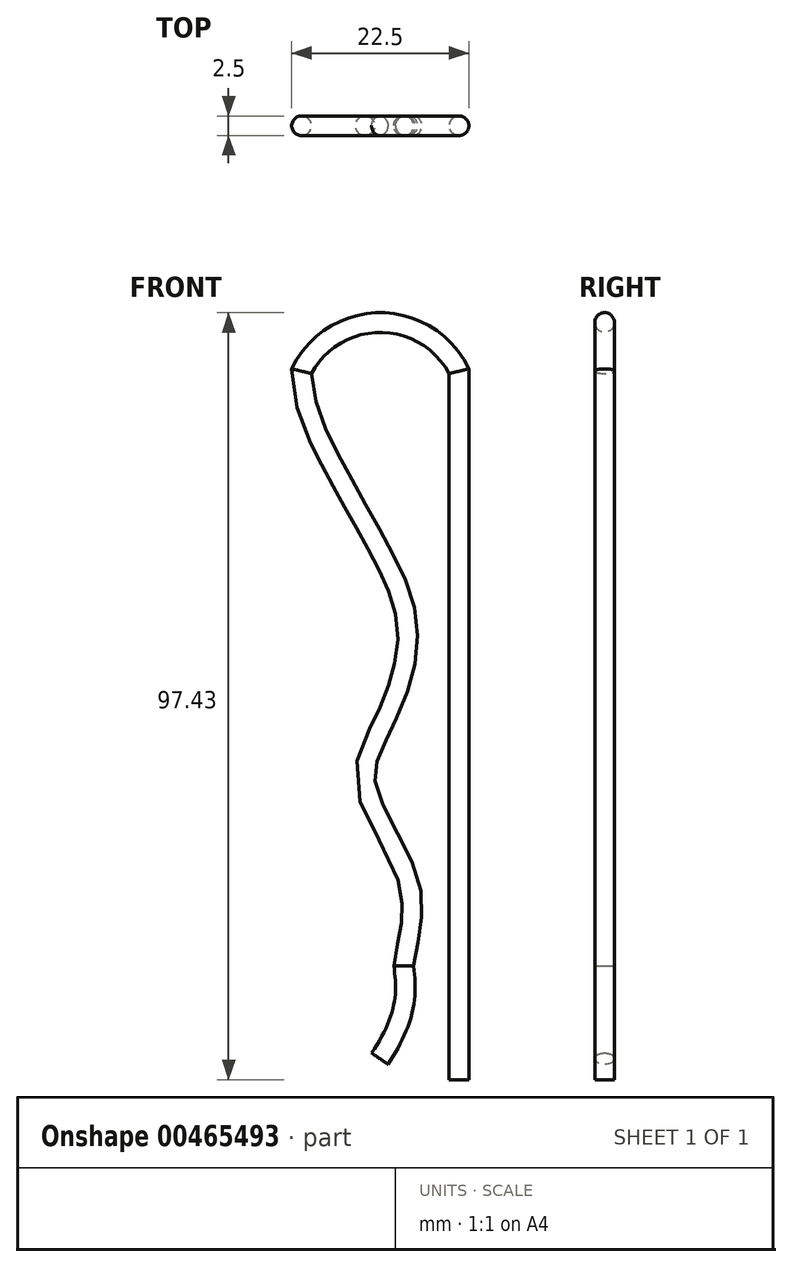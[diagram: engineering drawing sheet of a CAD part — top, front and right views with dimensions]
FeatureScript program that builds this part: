
annotation { "Feature Type Name" : "Feature", "Feature Type Description" : "" }
export const myFeature = defineFeature(function(context is Context, id is Id, definition is map)
    precondition{}
    {
        {
            var Q0;
            Q0=qCreatedBy(makeId("Front.planeOp"),FACE);
            var sketch = newSketch(context, id + "F0", { "sketchPlane" : qUnion([Q0])});
            skLineSegment(sketch, "E0", {"start": v(0, 0) * mm, "end": v(0, 90) * mm});
            skArc(sketch, "E1", {"start": v(0, 90) * mm, "mid": v(-10, 96.18) * mm, "end": v(-20, 90) * mm});
            skFitSpline(sketch, "E2", {"points": [v(-20, 90) * mm, v(-17.61, 81.2) * mm, v(-10.32, 67.77) * mm, v(-6.5, 56.56) * mm, v(-9.57, 45.36) * mm, v(-11.84, 37.38) * mm, v(-6.32, 24.93) * mm, v(-7.03, 14.46) * mm], "startDerivative": vector(0, -68.5) * mm, "endDerivative": vector(-11.48, -74.33) * mm});
            skFitSpline(sketch, "E3", {"points": [v(-7.03, 14.46) * mm, v(-7.03, 9.48) * mm, v(-10.07, 2.67) * mm], "startDerivative": vector(1.5, -10.95) * mm, "endDerivative": vector(-8.6, -12.4) * mm});
            skSolve(sketch);
        }
        {
            var Q0;
            Q0=qCreatedBy(makeId("Top.planeOp"),FACE);
            var sketch = newSketch(context, id + "F1", { "sketchPlane" : qUnion([Q0])});
            skCircle(sketch, "E4", {"center": v(0, 0) * mm, "radius": 1.25 * mm});
            skSolve(sketch);
        }
        {
            var Q0;
            Q0=makeQuery(id+"F1.imprint","IMPRINT",FACE,{"disambiguationData":[TD([[makeQuery(id+"F1.imprint","IMPRINT",EDGE,{"derivedFrom":sQuery(id+"F1.wireOp",EDGE,"E4")}),1.0]])]});
            var Q1;
            Q1 = qConstructionFilter(qBodyType(qCreatedBy(id + "F0" ,EDGE), BodyType.WIRE), ConstructionObject.NO);
            sweep(context, id + "F2", {"profiles" : qUnion([Q0]), "path" : qUnion([Q1])});
        }
    });
